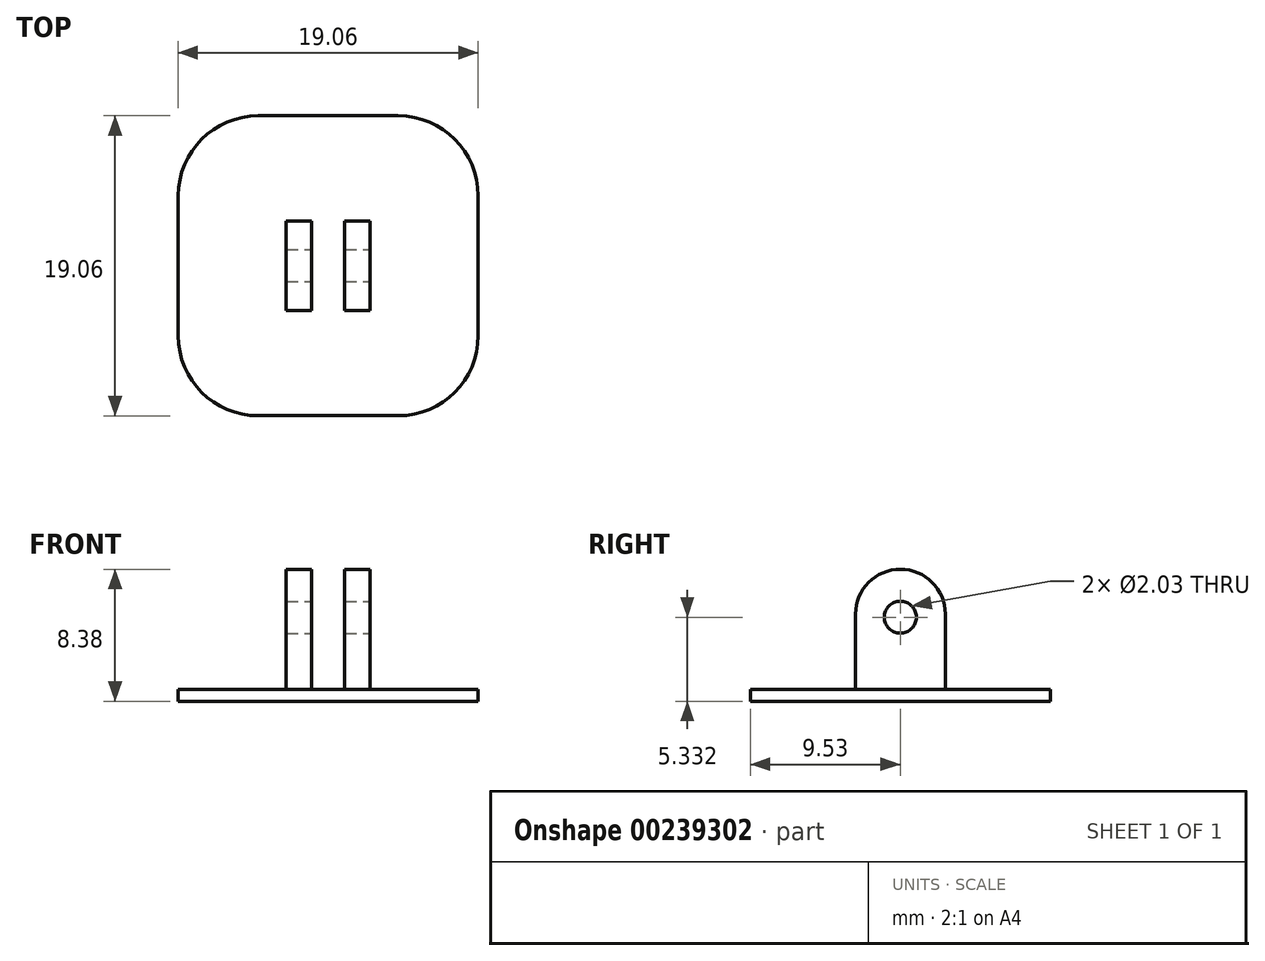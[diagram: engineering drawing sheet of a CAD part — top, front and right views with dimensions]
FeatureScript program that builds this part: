
annotation { "Feature Type Name" : "Feature", "Feature Type Description" : "" }
export const myFeature = defineFeature(function(context is Context, id is Id, definition is map)
    precondition{}
    {
        {
            var Q0;
            Q0=qCreatedBy(makeId("Right.planeOp"),FACE);
            var sketch = newSketch(context, id + "F0", { "sketchPlane" : qUnion([Q0])});
            skLineSegment(sketch, "E0", {"start": v(-2.85, 0) * mm, "end": v(-2.85, 4.77) * mm});
            skArc(sketch, "E1", {"start": v(-2.85, 4.77) * mm, "mid": v(-2.02, 6.79) * mm, "end": v(0, 7.62) * mm});
            skCircle(sketch, "E2", {"center": v(0, 4.57) * mm, "radius": 1.02 * mm});
            skArc(sketch, "E3.MirrorCS", {"start": v(2.85, 4.77) * mm, "mid": v(2.02, 6.79) * mm, "end": v(0, 7.62) * mm});
            skLineSegment(sketch, "E4.MirrorCS", {"start": v(2.85, 0) * mm, "end": v(2.85, 4.77) * mm});
            skLineSegment(sketch, "E5", {"start": v(-2.85, 0) * mm, "end": v(2.85, 0) * mm});
            skSolve(sketch);
        }
        {
            var Q0;
            Q0 = qSketchRegion(id + "F0", true);
            extrude(context, id + "F1", {"entities" : qUnion([Q0]), "endBound" : BoundingType.SYMMETRIC, "oppositeDirection" : true, "depth" : 5.33 * mm});
        }
        {
            var Q0;
            Q0=makeQuery(id+"F1.opExtrude","SWEPT_FACE",FACE,{"disambiguationData":[OSD([sQuery(id+"F0.wireOp",EDGE,"E5")])]});
            var sketch = newSketch(context, id + "F2", { "sketchPlane" : qUnion([Q0])});
            skLineSegment(sketch, "E6.bottom", {"start": v(9.53, 9.53) * mm, "end": v(-9.52, 9.53) * mm});
            skLineSegment(sketch, "E6.top", {"start": v(9.52, -9.53) * mm, "end": v(-9.53, -9.53) * mm});
            skLineSegment(sketch, "E6.left", {"start": v(9.53, 9.53) * mm, "end": v(9.52, -9.52) * mm});
            skLineSegment(sketch, "E6.right", {"start": v(-9.52, 9.53) * mm, "end": v(-9.53, -9.53) * mm});
            skPoint(sketch, "E6.middle", {"position": v(0, 0) * mm});
            skSolve(sketch);
        }
        {
            var Q0;
            Q0 = qSketchRegion(id + "F2", true);
            extrude(context, id + "F3", {"entities" : qUnion([Q0]), "operationType" : NewBodyOperationType.ADD, "depth" : 0.76 * mm});
        }
        {
            var Q0;
            Q0=qCreatedBy(makeId("Front.planeOp"),FACE);
            var sketch = newSketch(context, id + "F4", { "sketchPlane" : qUnion([Q0])});
            skLineSegment(sketch, "E7", {"start": v(-1.05, 0) * mm, "end": v(1.05, 0) * mm});
            skLineSegment(sketch, "E8", {"start": v(1.05, 0) * mm, "end": v(1.05, 12.7) * mm});
            skLineSegment(sketch, "E9", {"start": v(1.05, 12.7) * mm, "end": v(-1.05, 12.7) * mm});
            skLineSegment(sketch, "E10", {"start": v(-1.05, 12.7) * mm, "end": v(-1.05, 0) * mm});
            skSolve(sketch);
        }
        {
            var Q0;
            Q0 = qSketchRegion(id + "F4", true);
            extrude(context, id + "F5", {"entities" : qUnion([Q0]), "operationType" : NewBodyOperationType.REMOVE, "endBound" : BoundingType.SYMMETRIC, "oppositeDirection" : true, "depth" : 25.4 * mm});
        }
        {
            var Q0;
            Q0=makeQuery(id+"F3.opExtrude","SWEPT_EDGE",EDGE,{"disambiguationData":[OSD([sQuery(id+"F2.wireOp",EDGE,"E6.top"),sQuery(id+"F2.wireOp",EDGE,"E6.left")])]});
            var Q1;
            Q1=makeQuery(id+"F3.opExtrude","SWEPT_EDGE",EDGE,{"disambiguationData":[OSD([sQuery(id+"F2.wireOp",EDGE,"E6.top"),sQuery(id+"F2.wireOp",EDGE,"E6.right")])]});
            var Q2;
            Q2=makeQuery(id+"F3.opExtrude","SWEPT_EDGE",EDGE,{"disambiguationData":[OSD([sQuery(id+"F2.wireOp",EDGE,"E6.bottom"),sQuery(id+"F2.wireOp",EDGE,"E6.left")])]});
            var Q3;
            Q3=makeQuery(id+"F3.opExtrude","SWEPT_EDGE",EDGE,{"disambiguationData":[OSD([sQuery(id+"F2.wireOp",EDGE,"E6.bottom"),sQuery(id+"F2.wireOp",EDGE,"E6.right")])]});
            fillet(context, id + "F6", {"entities" : qUnion([Q0, Q1, Q2, Q3]), "radius" : 5.08 * mm, "tangentPropagation" : true, "allowEdgeOverflow" : false});
        }
    });
